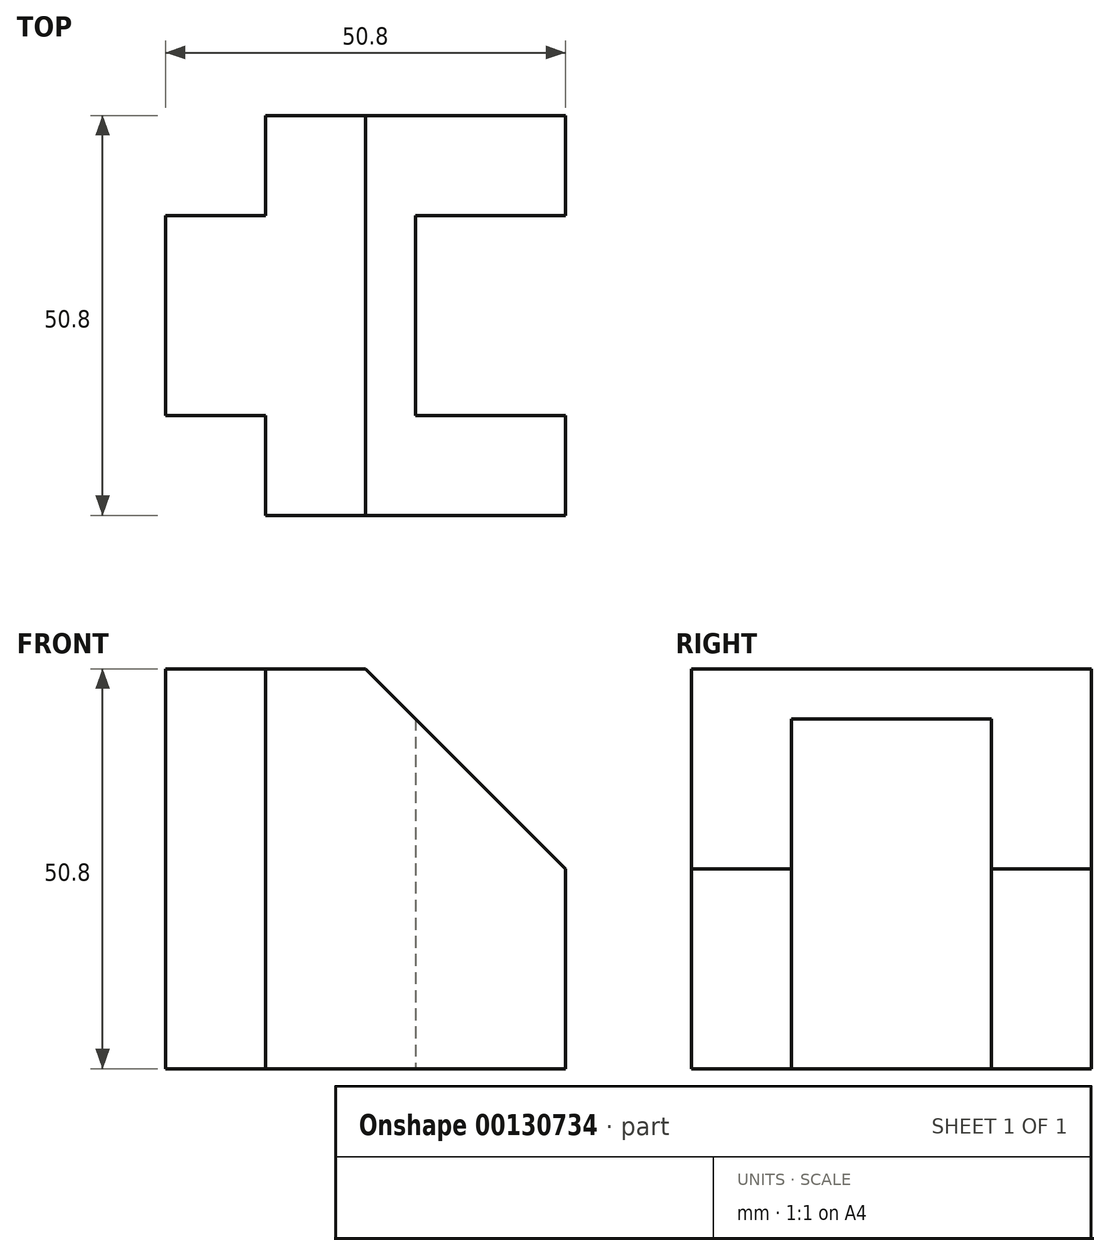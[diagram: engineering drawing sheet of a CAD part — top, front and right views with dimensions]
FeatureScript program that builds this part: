
annotation { "Feature Type Name" : "Feature", "Feature Type Description" : "" }
export const myFeature = defineFeature(function(context is Context, id is Id, definition is map)
    precondition{}
    {
        {
            var Q0;
            Q0=qCreatedBy(makeId("Top.planeOp"),FACE);
            var sketch = newSketch(context, id + "F0", { "sketchPlane" : qUnion([Q0])});
            skLineSegment(sketch, "E0", {"start": v(0, 0) * mm, "end": v(0, 50.8) * mm});
            skLineSegment(sketch, "E1", {"start": v(0, 50.8) * mm, "end": v(25.4, 50.8) * mm});
            skLineSegment(sketch, "E2", {"start": v(25.4, 50.8) * mm, "end": v(25.4, 38.1) * mm});
            skLineSegment(sketch, "E3", {"start": v(25.4, 38.1) * mm, "end": v(6.35, 38.1) * mm});
            skLineSegment(sketch, "E4", {"start": v(6.35, 38.1) * mm, "end": v(6.35, 12.7) * mm});
            skLineSegment(sketch, "E5", {"start": v(6.35, 12.7) * mm, "end": v(25.4, 12.7) * mm});
            skLineSegment(sketch, "E6", {"start": v(25.4, 12.7) * mm, "end": v(25.4, 0) * mm});
            skLineSegment(sketch, "E7", {"start": v(25.4, 0) * mm, "end": v(0, 0) * mm});
            skLineSegment(sketch, "E8", {"start": v(0, 50.8) * mm, "end": v(-12.7, 50.8) * mm});
            skLineSegment(sketch, "E9", {"start": v(-12.7, 50.8) * mm, "end": v(-12.7, 38.1) * mm});
            skLineSegment(sketch, "E10", {"start": v(-12.7, 38.1) * mm, "end": v(-25.4, 38.1) * mm});
            skLineSegment(sketch, "E11", {"start": v(-25.4, 38.1) * mm, "end": v(-25.4, 12.7) * mm});
            skLineSegment(sketch, "E12", {"start": v(-25.4, 12.7) * mm, "end": v(-12.7, 12.7) * mm});
            skLineSegment(sketch, "E13", {"start": v(-12.7, 12.7) * mm, "end": v(-12.7, 0) * mm});
            skLineSegment(sketch, "E14", {"start": v(-12.7, 0) * mm, "end": v(0, 0) * mm});
            skSolve(sketch);
        }
        {
            var Q0;
            Q0 = qSketchRegion(id + "F0", true);
            extrude(context, id + "F1", {"entities" : qUnion([Q0]), "depth" : 50.8 * mm});
        }
        {
            var Q0;
            Q0=makeQuery(id+"F1.opExtrude","SWEPT_FACE",FACE,{"disambiguationData":[OSD([sQuery(id+"F0.wireOp",EDGE,"E7"),sQuery(id+"F0.wireOp",EDGE,"E14")])]});
            var sketch = newSketch(context, id + "F2", { "sketchPlane" : qUnion([Q0])});
            skLineSegment(sketch, "E15", {"start": v(0, 50.8) * mm, "end": v(25.4, 25.4) * mm});
            skLineSegment(sketch, "E16", {"start": v(25.4, 25.4) * mm, "end": v(25.4, 50.8) * mm});
            skLineSegment(sketch, "E17", {"start": v(25.4, 50.8) * mm, "end": v(0, 50.8) * mm});
            skSolve(sketch);
        }
        {
            var Q0;
            Q0 = qSketchRegion(id + "F2", true);
            extrude(context, id + "F3", {"entities" : qUnion([Q0]), "operationType" : NewBodyOperationType.REMOVE, "endBound" : BoundingType.THROUGH_ALL, "oppositeDirection" : true, "depth" : 25.4 * mm});
        }
    });
